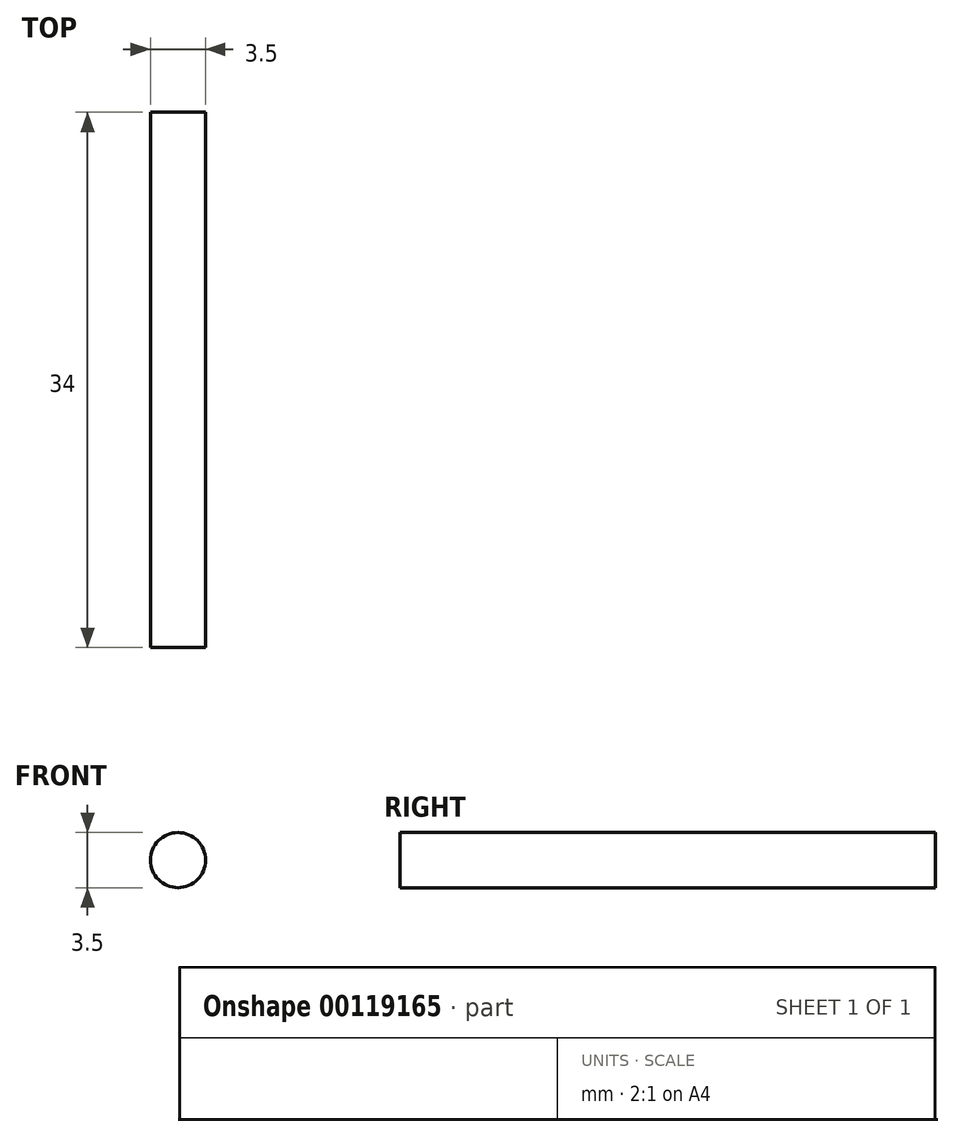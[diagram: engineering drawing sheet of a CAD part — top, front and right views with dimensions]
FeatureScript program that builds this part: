
annotation { "Feature Type Name" : "Feature", "Feature Type Description" : "" }
export const myFeature = defineFeature(function(context is Context, id is Id, definition is map)
    precondition{}
    {
        {
            var Q0;
            Q0=qCreatedBy(makeId("Front.planeOp"),FACE);
            var sketch = newSketch(context, id + "F0", { "sketchPlane" : qUnion([Q0])});
            skCircle(sketch, "E0", {"center": v(0, 0) * mm, "radius": 1.75 * mm});
            skSolve(sketch);
        }
        {
            var Q0;
            Q0=makeQuery(id+"F0.imprint","IMPRINT",FACE,{"disambiguationData":[TD([[makeQuery(id+"F0.imprint","IMPRINT",EDGE,{"derivedFrom":sQuery(id+"F0.wireOp",EDGE,"E0")}),1.0]])]});
            extrude(context, id + "F1", {"entities" : qUnion([Q0]), "depth" : 34 * mm});
        }
    });
